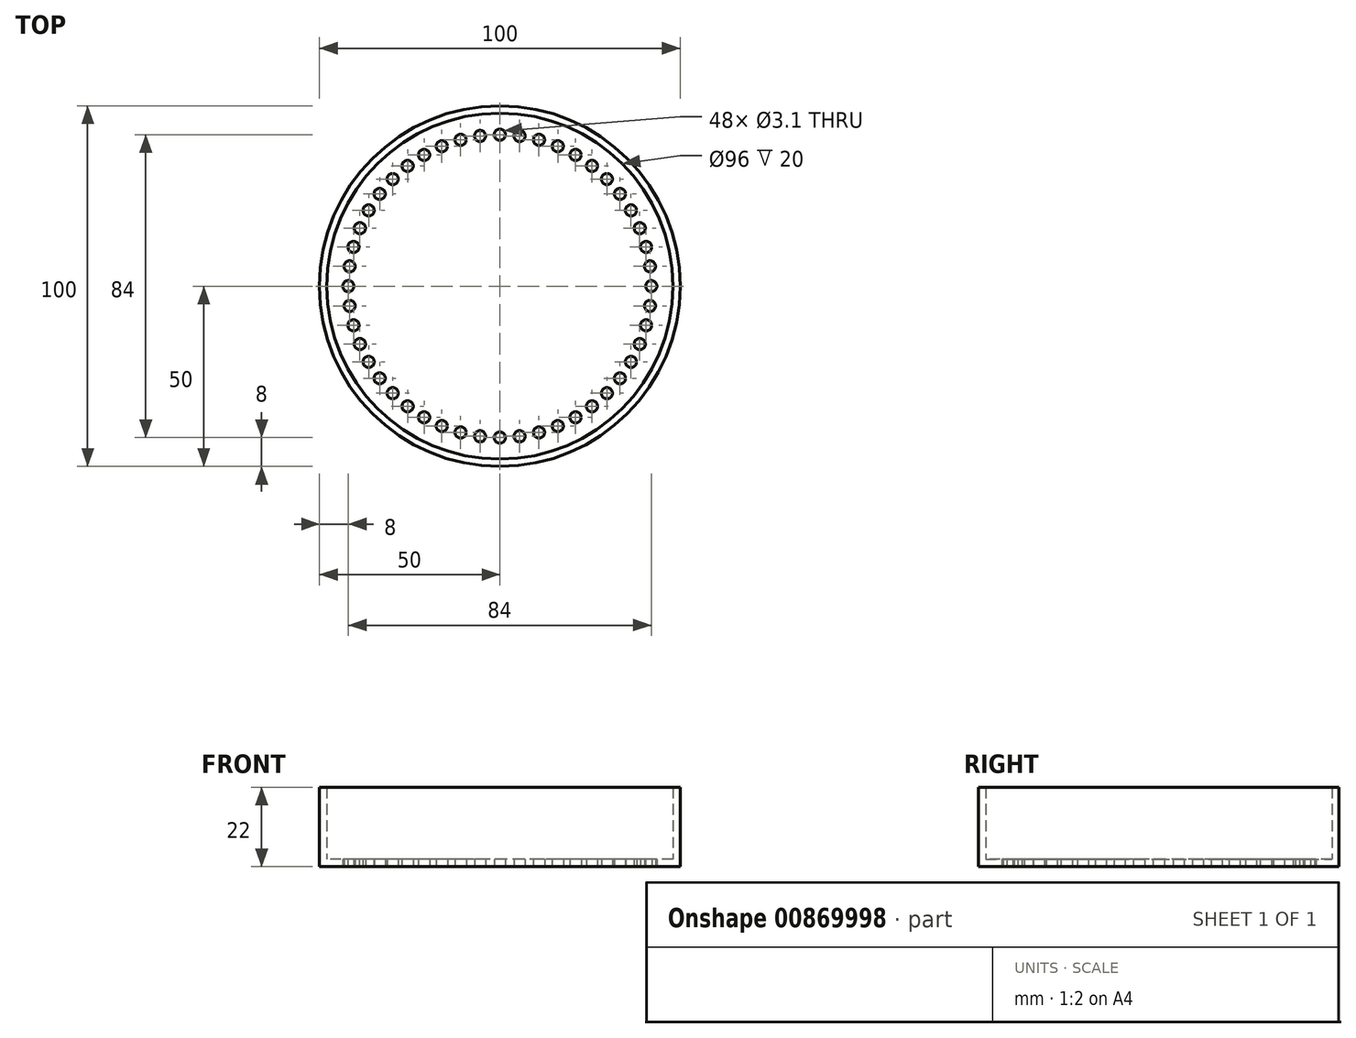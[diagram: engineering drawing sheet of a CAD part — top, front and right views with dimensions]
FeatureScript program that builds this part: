
annotation { "Feature Type Name" : "Feature", "Feature Type Description" : "" }
export const myFeature = defineFeature(function(context is Context, id is Id, definition is map)
    precondition{}
    {
        {
            var Q0;
            Q0=qCreatedBy(makeId("Top.planeOp"),FACE);
            var sketch = newSketch(context, id + "F0", { "sketchPlane" : qUnion([Q0])});
            skCircle(sketch, "E0", {"center": v(0, 0) * mm, "radius": 50 * mm});
            skCircle(sketch, "E1", {"center": v(-42, 0) * mm, "radius": 1.55 * mm});
            skCircle(sketch, "E2.1.0", {"center": v(-41.64, -5.48) * mm, "radius": 1.55 * mm});
            skCircle(sketch, "E2.2.0", {"center": v(-40.57, -10.87) * mm, "radius": 1.55 * mm});
            skCircle(sketch, "E2.3.0", {"center": v(-38.8, -16.07) * mm, "radius": 1.55 * mm});
            skCircle(sketch, "E2.4.0", {"center": v(-36.37, -21) * mm, "radius": 1.55 * mm});
            skCircle(sketch, "E2.5.0", {"center": v(-33.32, -25.57) * mm, "radius": 1.55 * mm});
            skCircle(sketch, "E2.6.0", {"center": v(-29.7, -29.7) * mm, "radius": 1.55 * mm});
            skCircle(sketch, "E2.7.0", {"center": v(-25.57, -33.32) * mm, "radius": 1.55 * mm});
            skCircle(sketch, "E2.8.0", {"center": v(-21, -36.37) * mm, "radius": 1.55 * mm});
            skCircle(sketch, "E2.9.0", {"center": v(-16.07, -38.8) * mm, "radius": 1.55 * mm});
            skCircle(sketch, "E2.10.0", {"center": v(-10.87, -40.57) * mm, "radius": 1.55 * mm});
            skCircle(sketch, "E2.11.0", {"center": v(-5.48, -41.64) * mm, "radius": 1.55 * mm});
            skCircle(sketch, "E2.12.0", {"center": v(0, -42) * mm, "radius": 1.55 * mm});
            skCircle(sketch, "E2.13.0", {"center": v(5.48, -41.64) * mm, "radius": 1.55 * mm});
            skCircle(sketch, "E2.14.0", {"center": v(10.87, -40.57) * mm, "radius": 1.55 * mm});
            skCircle(sketch, "E2.15.0", {"center": v(16.07, -38.8) * mm, "radius": 1.55 * mm});
            skCircle(sketch, "E2.16.0", {"center": v(21, -36.37) * mm, "radius": 1.55 * mm});
            skCircle(sketch, "E2.17.0", {"center": v(25.57, -33.32) * mm, "radius": 1.55 * mm});
            skCircle(sketch, "E2.18.0", {"center": v(29.7, -29.7) * mm, "radius": 1.55 * mm});
            skCircle(sketch, "E2.19.0", {"center": v(33.32, -25.57) * mm, "radius": 1.55 * mm});
            skCircle(sketch, "E2.20.0", {"center": v(36.37, -21) * mm, "radius": 1.55 * mm});
            skCircle(sketch, "E2.21.0", {"center": v(38.8, -16.07) * mm, "radius": 1.55 * mm});
            skCircle(sketch, "E2.22.0", {"center": v(40.57, -10.87) * mm, "radius": 1.55 * mm});
            skCircle(sketch, "E2.23.0", {"center": v(41.64, -5.48) * mm, "radius": 1.55 * mm});
            skCircle(sketch, "E2.24.0", {"center": v(42, 0) * mm, "radius": 1.55 * mm});
            skCircle(sketch, "E2.25.0", {"center": v(41.64, 5.48) * mm, "radius": 1.55 * mm});
            skCircle(sketch, "E2.26.0", {"center": v(40.57, 10.87) * mm, "radius": 1.55 * mm});
            skCircle(sketch, "E2.27.0", {"center": v(38.8, 16.07) * mm, "radius": 1.55 * mm});
            skCircle(sketch, "E2.28.0", {"center": v(36.37, 21) * mm, "radius": 1.55 * mm});
            skCircle(sketch, "E2.29.0", {"center": v(33.32, 25.57) * mm, "radius": 1.55 * mm});
            skCircle(sketch, "E2.30.0", {"center": v(29.7, 29.7) * mm, "radius": 1.55 * mm});
            skCircle(sketch, "E2.31.0", {"center": v(25.57, 33.32) * mm, "radius": 1.55 * mm});
            skCircle(sketch, "E2.32.0", {"center": v(21, 36.37) * mm, "radius": 1.55 * mm});
            skCircle(sketch, "E2.33.0", {"center": v(16.07, 38.8) * mm, "radius": 1.55 * mm});
            skCircle(sketch, "E2.34.0", {"center": v(10.87, 40.57) * mm, "radius": 1.55 * mm});
            skCircle(sketch, "E2.35.0", {"center": v(5.48, 41.64) * mm, "radius": 1.55 * mm});
            skCircle(sketch, "E2.36.0", {"center": v(0, 42) * mm, "radius": 1.55 * mm});
            skCircle(sketch, "E2.37.0", {"center": v(-5.48, 41.64) * mm, "radius": 1.55 * mm});
            skCircle(sketch, "E2.38.0", {"center": v(-10.87, 40.57) * mm, "radius": 1.55 * mm});
            skCircle(sketch, "E2.39.0", {"center": v(-16.07, 38.8) * mm, "radius": 1.55 * mm});
            skCircle(sketch, "E2.40.0", {"center": v(-21, 36.37) * mm, "radius": 1.55 * mm});
            skCircle(sketch, "E2.41.0", {"center": v(-25.57, 33.32) * mm, "radius": 1.55 * mm});
            skCircle(sketch, "E2.42.0", {"center": v(-29.7, 29.7) * mm, "radius": 1.55 * mm});
            skCircle(sketch, "E2.43.0", {"center": v(-33.32, 25.57) * mm, "radius": 1.55 * mm});
            skCircle(sketch, "E2.44.0", {"center": v(-36.37, 21) * mm, "radius": 1.55 * mm});
            skCircle(sketch, "E2.45.0", {"center": v(-38.8, 16.07) * mm, "radius": 1.55 * mm});
            skCircle(sketch, "E2.46.0", {"center": v(-40.57, 10.87) * mm, "radius": 1.55 * mm});
            skCircle(sketch, "E2.47.0", {"center": v(-41.64, 5.48) * mm, "radius": 1.55 * mm});
            skSolve(sketch);
        }
        {
            var Q0;
            Q0=makeQuery(id+"F0.imprint","IMPRINT",FACE,{"disambiguationData":[TD([[makeQuery(id+"F0.imprint","IMPRINT",EDGE,{"derivedFrom":sQuery(id+"F0.wireOp",EDGE,"E0")}),1.0]])]});
            extrude(context, id + "F1", {"entities" : qUnion([Q0]), "depth" : 2 * mm, "offsetDistance" : 25 * mm});
        }
        {
            var Q0;
            Q0=makeQuery(id+"F1.opExtrude","CAP_FACE",FACE,{"disambiguationData":[OSD([sQuery(id+"F0.wireOp",EDGE,"E0"),sQuery(id+"F0.wireOp",EDGE,"E1"),sQuery(id+"F0.wireOp",EDGE,"E2.1.0"),sQuery(id+"F0.wireOp",EDGE,"E2.2.0"),sQuery(id+"F0.wireOp",EDGE,"E2.3.0"),sQuery(id+"F0.wireOp",EDGE,"E2.4.0"),sQuery(id+"F0.wireOp",EDGE,"E2.5.0"),sQuery(id+"F0.wireOp",EDGE,"E2.6.0"),sQuery(id+"F0.wireOp",EDGE,"E2.7.0"),sQuery(id+"F0.wireOp",EDGE,"E2.8.0"),sQuery(id+"F0.wireOp",EDGE,"E2.9.0"),sQuery(id+"F0.wireOp",EDGE,"E2.10.0"),sQuery(id+"F0.wireOp",EDGE,"E2.11.0"),sQuery(id+"F0.wireOp",EDGE,"E2.12.0"),sQuery(id+"F0.wireOp",EDGE,"E2.13.0"),sQuery(id+"F0.wireOp",EDGE,"E2.14.0"),sQuery(id+"F0.wireOp",EDGE,"E2.15.0"),sQuery(id+"F0.wireOp",EDGE,"E2.16.0"),sQuery(id+"F0.wireOp",EDGE,"E2.17.0"),sQuery(id+"F0.wireOp",EDGE,"E2.18.0"),sQuery(id+"F0.wireOp",EDGE,"E2.19.0"),sQuery(id+"F0.wireOp",EDGE,"E2.20.0"),sQuery(id+"F0.wireOp",EDGE,"E2.21.0"),sQuery(id+"F0.wireOp",EDGE,"E2.22.0"),sQuery(id+"F0.wireOp",EDGE,"E2.23.0"),sQuery(id+"F0.wireOp",EDGE,"E2.24.0"),sQuery(id+"F0.wireOp",EDGE,"E2.25.0"),sQuery(id+"F0.wireOp",EDGE,"E2.26.0"),sQuery(id+"F0.wireOp",EDGE,"E2.27.0"),sQuery(id+"F0.wireOp",EDGE,"E2.28.0"),sQuery(id+"F0.wireOp",EDGE,"E2.29.0"),sQuery(id+"F0.wireOp",EDGE,"E2.30.0"),sQuery(id+"F0.wireOp",EDGE,"E2.31.0"),sQuery(id+"F0.wireOp",EDGE,"E2.32.0"),sQuery(id+"F0.wireOp",EDGE,"E2.33.0"),sQuery(id+"F0.wireOp",EDGE,"E2.34.0"),sQuery(id+"F0.wireOp",EDGE,"E2.35.0"),sQuery(id+"F0.wireOp",EDGE,"E2.36.0"),sQuery(id+"F0.wireOp",EDGE,"E2.37.0"),sQuery(id+"F0.wireOp",EDGE,"E2.38.0"),sQuery(id+"F0.wireOp",EDGE,"E2.39.0"),sQuery(id+"F0.wireOp",EDGE,"E2.40.0"),sQuery(id+"F0.wireOp",EDGE,"E2.41.0"),sQuery(id+"F0.wireOp",EDGE,"E2.42.0"),sQuery(id+"F0.wireOp",EDGE,"E2.43.0"),sQuery(id+"F0.wireOp",EDGE,"E2.44.0"),sQuery(id+"F0.wireOp",EDGE,"E2.45.0"),sQuery(id+"F0.wireOp",EDGE,"E2.46.0"),sQuery(id+"F0.wireOp",EDGE,"E2.47.0")])],"isStart":false});
            var sketch = newSketch(context, id + "F2", { "sketchPlane" : qUnion([Q0])});
            skCircle(sketch, "E3", {"center": v(0, 0) * mm, "radius": 48 * mm});
            skSolve(sketch);
        }
        {
            var Q0;
            Q0=makeQuery(id+"F2.imprint","IMPRINT",FACE,{"disambiguationData":[TD([[makeQuery(id+"F2.imprint","IMPRINT",EDGE,{"derivedFrom":sQuery(id+"F2.wireOp",EDGE,"E3")}),-1.0]])]});
            extrude(context, id + "F3", {"entities" : qUnion([Q0]), "operationType" : NewBodyOperationType.ADD, "depth" : 20 * mm, "offsetDistance" : 25 * mm});
        }
    });
